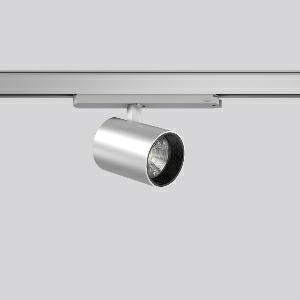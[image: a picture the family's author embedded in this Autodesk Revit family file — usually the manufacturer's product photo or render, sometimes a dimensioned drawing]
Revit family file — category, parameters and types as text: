
# Revit family: deecos_s_mini_track-in_742254_004_730_51d4
name_source: partatom
category: Lighting Fixtures
units: mm (PartAtom-declared; Revit-internal decimal feet)

## family parameters
Cut with Voids When Loaded = No
Host = Face
Light Source = No
Part Type = Normal
Room Calculation Point = No
Round Connector Dimension = Use Diameter
Shared = No

## types (1)
- DEECOS S mini track-in (1 x LED Modul 930, 2100 lm, 3000)
    Apparent Load = 20 VA
    Approval mark = CE
    CIE Flux Codes = 96 100 100 100 100
    Color Rendering = 90
    Color Temperature = 3000
    Default Elevation = 1800 mm
    Description = Series: DEECOS S mini track-in
LED surface-mounted projector in modern design with no visible cooling ribs. Housing: die-cast aluminium, powder-coated. Rotation range: 356°. Swivel range: 90°. Black plastic ring and recessed LED to prevent glare from the side. Optical assembly with lens made of plastic (polycarbonate) for the best homogeneous light distribution - can be changed without tools. Best colour rendering index Ra>90. With multi adaptor for 3-circuit tracks 230 V. Suitable for Track on ceiling, Wall track. Track-in driver integrated into the adapter. High quality converter without flickering and stroboscopic effect. With Casambi smart+free Bluetooth control for wireless network and operation using Android / iOS devices, free app available for download. The following accessories can be mounted without use of tools: interchangeable lenses, decorative glasses, honeycomb louvre, clear and frosted diffusers, white interchangeable plastic ring. 
Colour: silver
Diameter: 87 mm
Height: 135 mm
Lamp: LED
Socket: without socket
Colour temperature: 3000K
Colour rendering index (CRI): 92
System power: 20 W
Rated luminous flux: 2100 lm
Luminous efficiency: 105 lm/W
Control gear: Dimmable Bluetooth converter
Protection class: II
Type of protection: IP 20
    Height = 135 mm
    Lamp = 1 x LED Modul 930
    Lamp Light Flux = 2100 lm
    Lamp count = 1
    Length = 87 mm
    Lifetime = 50000 h
    Luminous efficacy = 105 lm/W
    Manufacturer = RZB
    ModVariant = No
    Model = 742254.004.730
    Mounting Place = Ceiling
    Mounting Type = Rail mounted
    Number of Poles = 1
    OnlyDefault = Yes
    Power Factor = 1
    Product Name = DEECOS S mini track-in
    Product group = Track mounted projectors
    ProductGroupID = 301
    Protection Class = Protection class II
    Protection Degree = IP 20
    RLX_Detail_Level = 1
    RLX_Emergency_Light_Flux = 0 lm
    RLX_Emergency_Type = 0
    RLX_Emergency_Type_DB = No
    RlxData = <blob elided: 36445 chars, md5=ba09bfe4>
    Socket = socket
    Standby Power = 0 W
    System Light Flux = 2100 lm
    System Power = 20 W
    Type Comments = Product without accessories
    Type Image = 742108.004.jpg
    URL = http://relux.com
    VarID = ---
    Voltage = 230 V
    Voltage Range = 220-240 V
    Weight = 0.00 kg
    Width = 0 mm  [stored 0 ft]

note: [stored X ft] marks values corroborated as IEEE doubles in the binary element streams (Revit-internal decimal feet)

## geometry (parser evidence)
native form markers: Blend x4, Sweep x13
no freeform markers — native parametric forms only
